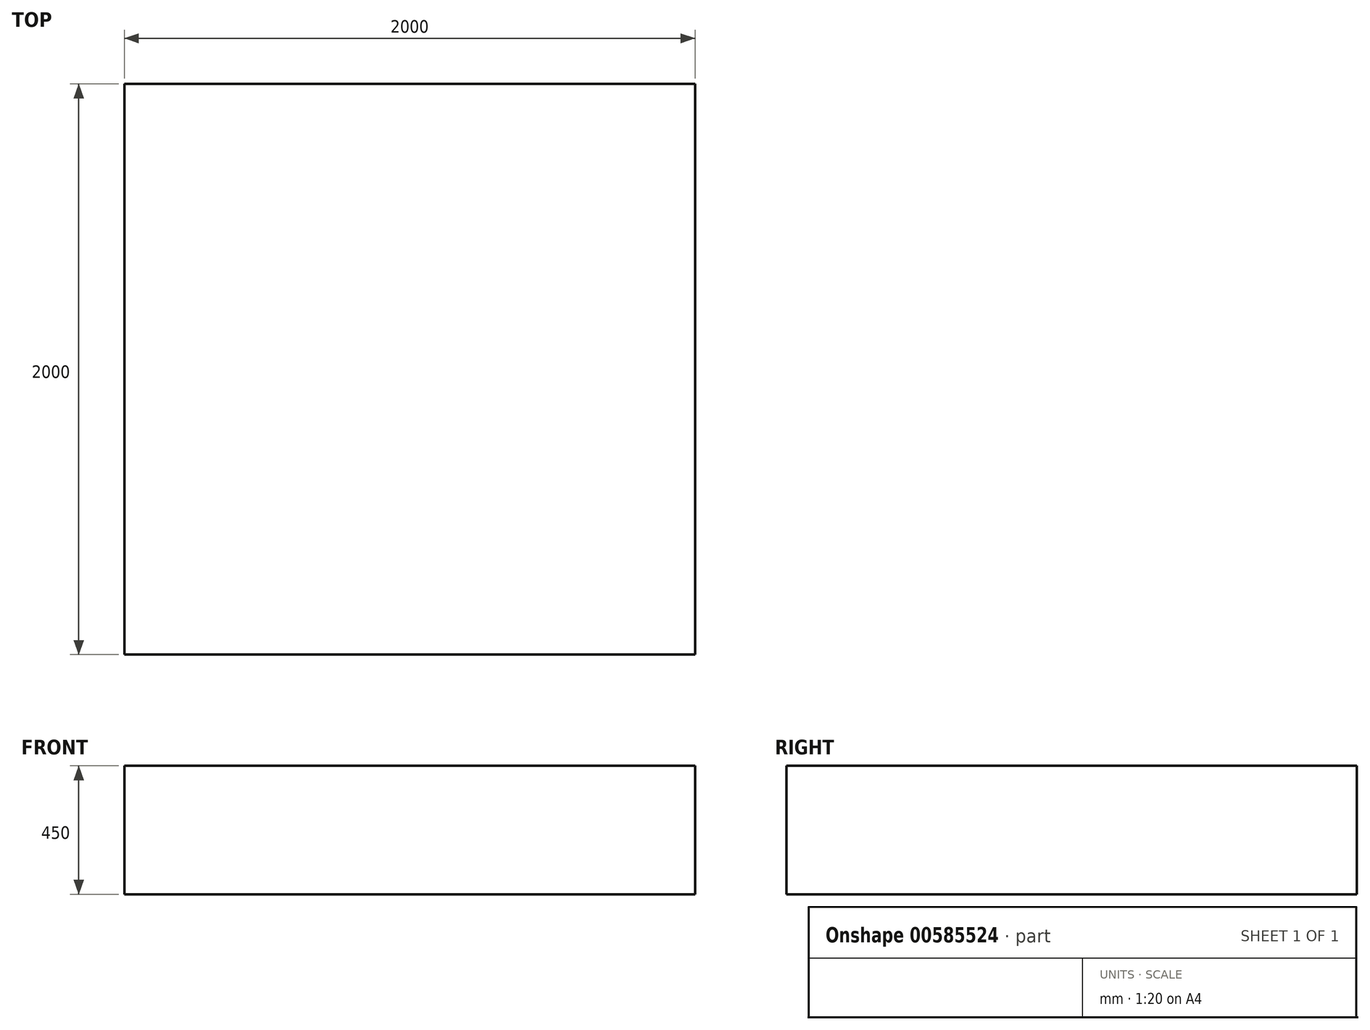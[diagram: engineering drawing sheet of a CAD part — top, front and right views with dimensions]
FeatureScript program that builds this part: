
annotation { "Feature Type Name" : "Feature", "Feature Type Description" : "" }
export const myFeature = defineFeature(function(context is Context, id is Id, definition is map)
    precondition{}
    {
        {
            var Q0;
            Q0=qCreatedBy(makeId("Top.planeOp"),FACE);
            var sketch = newSketch(context, id + "F0", { "sketchPlane" : qUnion([Q0])});
            skLineSegment(sketch, "E0.bottom", {"start": v(1000, 1000) * mm, "end": v(-1000, 1000) * mm});
            skLineSegment(sketch, "E0.top", {"start": v(1000, -1000) * mm, "end": v(-1000, -1000) * mm});
            skLineSegment(sketch, "E0.left", {"start": v(1000, 1000) * mm, "end": v(1000, -1000) * mm});
            skLineSegment(sketch, "E0.right", {"start": v(-1000, 1000) * mm, "end": v(-1000, -1000) * mm});
            skPoint(sketch, "E0.middle", {"position": v(0, 0) * mm});
            skSolve(sketch);
        }
        {
            var Q0;
            Q0 = qSketchRegion(id + "F0", true);
            extrude(context, id + "F1", {"entities" : qUnion([Q0]), "depth" : 450 * mm, "offsetDistance" : 25 * mm});
        }
    });
